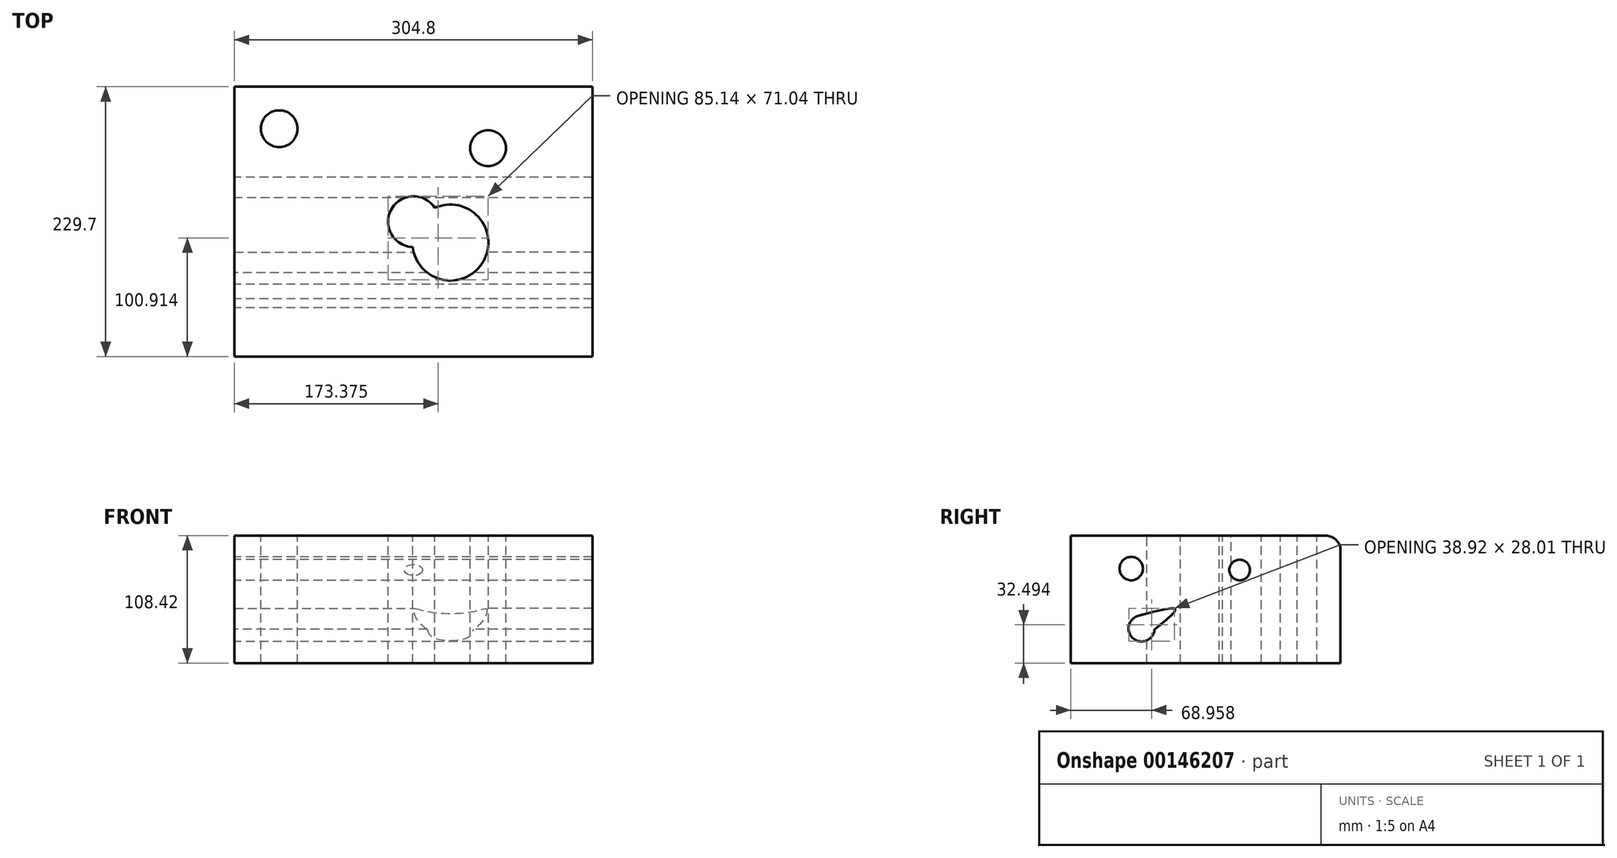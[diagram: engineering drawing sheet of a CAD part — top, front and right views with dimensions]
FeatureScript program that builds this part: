
annotation { "Feature Type Name" : "Feature", "Feature Type Description" : "" }
export const myFeature = defineFeature(function(context is Context, id is Id, definition is map)
    precondition{}
    {
        {
            var Q0;
            Q0=qCreatedBy(makeId("Right.planeOp"),FACE);
            var sketch = newSketch(context, id + "F0", { "sketchPlane" : qUnion([Q0])});
            skLineSegment(sketch, "E0.bottom", {"start": v(114.85, -54.21) * mm, "end": v(-114.85, -54.21) * mm});
            skLineSegment(sketch, "E0.top", {"start": v(114.85, 54.21) * mm, "end": v(-114.85, 54.21) * mm});
            skLineSegment(sketch, "E0.left", {"start": v(114.85, -54.21) * mm, "end": v(114.85, 54.21) * mm});
            skLineSegment(sketch, "E0.right", {"start": v(-114.85, -54.21) * mm, "end": v(-114.85, 54.21) * mm});
            skPoint(sketch, "E0.middle", {"position": v(0, 0) * mm});
            skCircle(sketch, "E1", {"center": v(-63.3, 26.18) * mm, "radius": 9.94 * mm});
            skCircle(sketch, "E2", {"center": v(28.99, 25) * mm, "radius": 8.78 * mm});
            skArc(sketch, "E3", {"start": v(-57.38, -14.05) * mm, "mid": v(-61.6, -33.28) * mm, "end": v(-43.48, -25.59) * mm});
            skFitSpline(sketch, "E4", {"points": [v(-57.38, -14.05) * mm, v(-26.03, -8.43) * mm, v(-43.48, -25.59) * mm], "startDerivative": vector(84.47, 23.14) * mm, "endDerivative": vector(-59.83, -47.77) * mm});
            skSolve(sketch);
        }
        {
            var Q0;
            Q0=makeQuery(id+"F0.imprint","IMPRINT",FACE,{"disambiguationData":[TD([[makeQuery(id+"F0.imprint","IMPRINT",EDGE,{"derivedFrom":sQuery(id+"F0.wireOp",EDGE,"E0.bottom")}),-1.0]])]});
            extrude(context, id + "F1", {"entities" : qUnion([Q0]), "depth" : 304.8 * mm, "symmetric" : true});
        }
        {
            var Q0;
            Q0=makeQuery(id+"F1.opExtrude","SWEPT_FACE",FACE,{"disambiguationData":[OSD([sQuery(id+"F0.wireOp",EDGE,"E0.top")])]});
            var sketch = newSketch(context, id + "F2", { "sketchPlane" : qUnion([Q0])});
            skCircle(sketch, "E5", {"center": v(-114.3, 79.14) * mm, "radius": 15.64 * mm});
            skCircle(sketch, "E6", {"center": v(63.5, 62.58) * mm, "radius": 15.3 * mm});
            skCircle(sketch, "E7", {"center": v(31.44, -17.78) * mm, "radius": 32.31 * mm});
            skCircle(sketch, "E8", {"center": v(0, 0) * mm, "radius": 21.6 * mm});
            skSolve(sketch);
        }
        {
            var Q0;
            Q0 = qSketchRegion(id + "F2", true);
            extrude(context, id + "F3", {"entities" : qUnion([Q0]), "operationType" : NewBodyOperationType.REMOVE, "endBound" : BoundingType.THROUGH_ALL, "oppositeDirection" : true, "depth" : 25.4 * mm});
        }
        {
            var Q0;
            Q0=makeQuery(id+"F1.opExtrude","SWEPT_EDGE",EDGE,{"disambiguationData":[OSD([sQuery(id+"F0.wireOp",EDGE,"E0.top"),sQuery(id+"F0.wireOp",EDGE,"E0.left")])]});
            fillet(context, id + "F4", {"entities" : qUnion([Q0]), "radius" : 12.7 * mm, "tangentPropagation" : true, "allowEdgeOverflow" : false});
        }
    });
